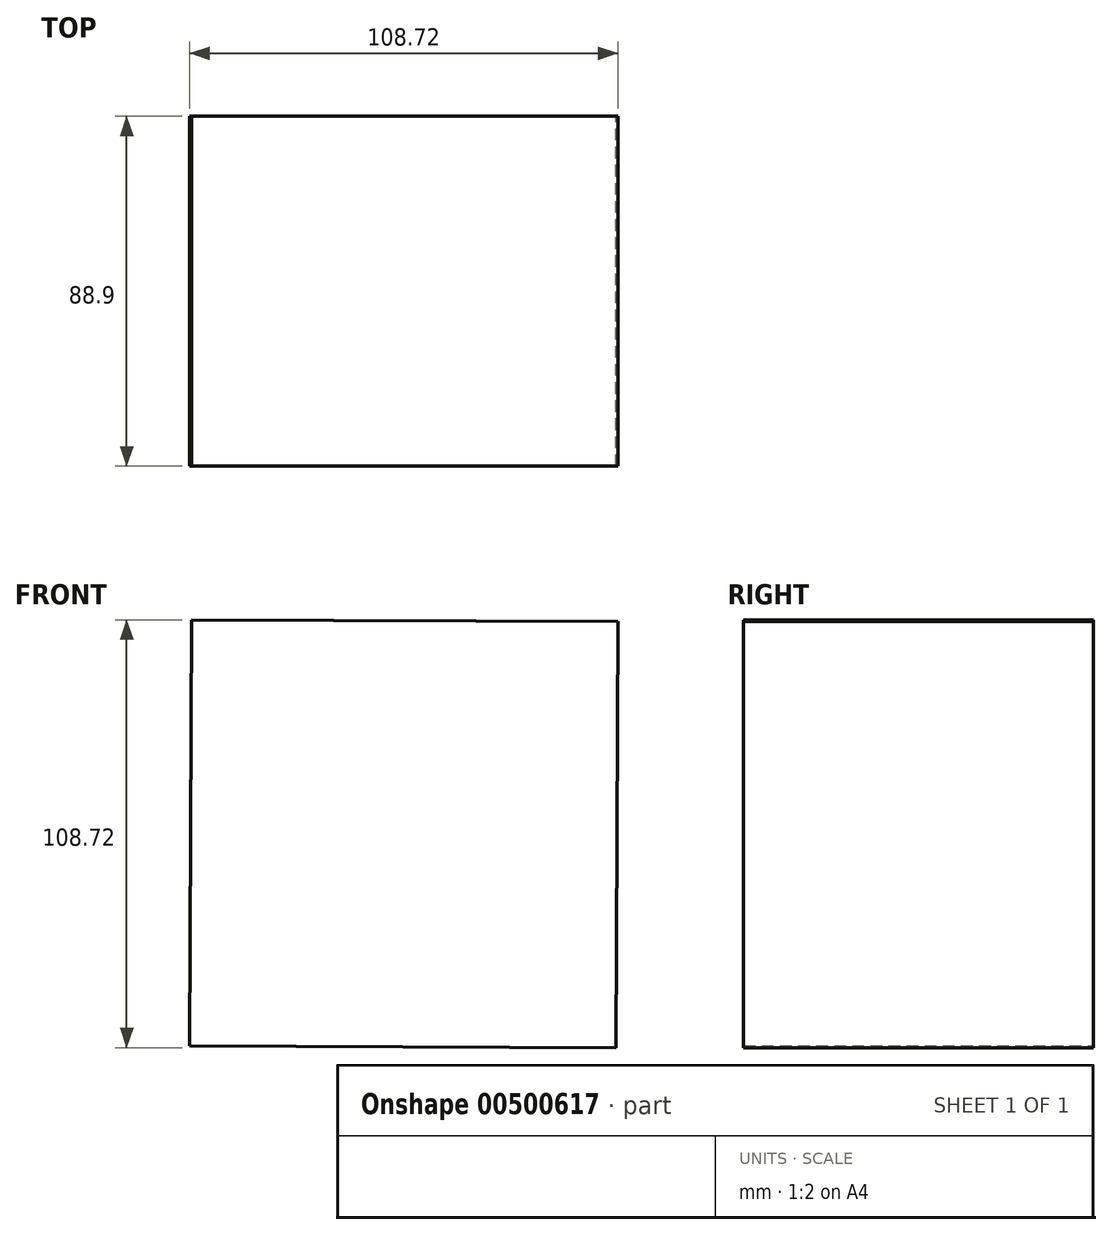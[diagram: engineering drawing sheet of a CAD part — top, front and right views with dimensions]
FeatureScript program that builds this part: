
annotation { "Feature Type Name" : "Feature", "Feature Type Description" : "" }
export const myFeature = defineFeature(function(context is Context, id is Id, definition is map)
    precondition{}
    {
        {
            var Q0;
            Q0=qCreatedBy(makeId("Front.planeOp"),FACE);
            var sketch = newSketch(context, id + "F0", { "sketchPlane" : qUnion([Q0])});
            skCircle(sketch, "E0.cCircle", {"center": v(0, 0) * mm, "radius": 76.57 * mm, "construction": true});
            skLineSegment(sketch, "E0.0", {"start": v(54.36, 53.92) * mm, "end": v(53.92, -54.36) * mm});
            skLineSegment(sketch, "E0.1", {"start": v(53.92, -54.36) * mm, "end": v(-54.36, -53.92) * mm});
            skLineSegment(sketch, "E0.2", {"start": v(-54.36, -53.92) * mm, "end": v(-53.92, 54.36) * mm});
            skLineSegment(sketch, "E0.3", {"start": v(-53.92, 54.36) * mm, "end": v(54.36, 53.92) * mm});
            skSolve(sketch);
        }
        {
            var Q0;
            Q0=makeQuery(id+"F0.imprint","IMPRINT",FACE,{"disambiguationData":[TD([[makeQuery(id+"F0.imprint","IMPRINT",EDGE,{"derivedFrom":sQuery(id+"F0.wireOp",EDGE,"E0.0")}),-1.0]])]});
            extrude(context, id + "F1", {"entities" : qUnion([Q0]), "depth" : 88.9 * mm});
        }
    });
